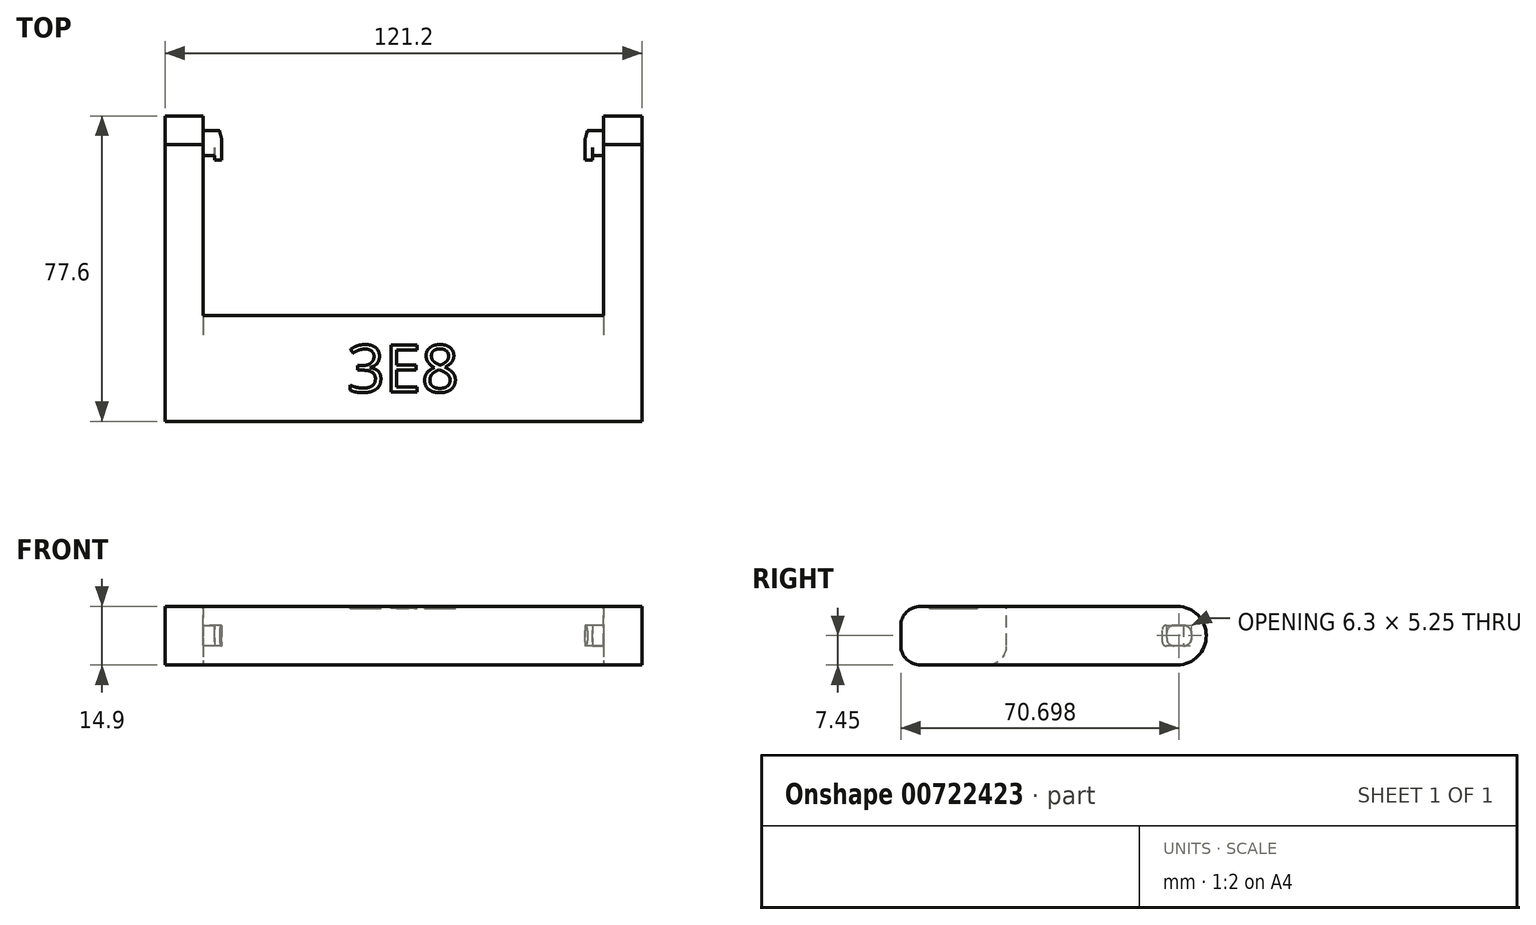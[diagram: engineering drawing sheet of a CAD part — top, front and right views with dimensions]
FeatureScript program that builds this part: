
annotation { "Feature Type Name" : "Feature", "Feature Type Description" : "" }
export const myFeature = defineFeature(function(context is Context, id is Id, definition is map)
    precondition{}
    {
        {
            var Q0;
            Q0=qCreatedBy(makeId("Top.planeOp"),FACE);
            var sketch = newSketch(context, id + "F0", { "sketchPlane" : qUnion([Q0])});
            skLineSegment(sketch, "E0.bottom", {"start": v(60.6, -38.8) * mm, "end": v(-60.6, -38.8) * mm});
            skLineSegment(sketch, "E0.top", {"start": v(60.6, 38.8) * mm, "end": v(-60.6, 38.8) * mm});
            skLineSegment(sketch, "E0.left", {"start": v(60.6, -38.8) * mm, "end": v(60.6, 38.8) * mm});
            skLineSegment(sketch, "E0.right", {"start": v(-60.6, -38.8) * mm, "end": v(-60.6, 38.8) * mm});
            skPoint(sketch, "E0.middle", {"position": v(0, 0) * mm});
            skSolve(sketch);
        }
        {
            var Q0;
            Q0 = qSketchRegion(id + "F0", true);
            extrude(context, id + "F1", {"entities" : qUnion([Q0]), "depth" : 14.9 * mm, "offsetDistance" : 25 * mm});
        }
        {
            var Q0;
            Q0=makeQuery(id+"F1.opExtrude","CAP_FACE",FACE,{"disambiguationData":[OSD([sQuery(id+"F0.wireOp",EDGE,"E0.bottom"),sQuery(id+"F0.wireOp",EDGE,"E0.top"),sQuery(id+"F0.wireOp",EDGE,"E0.left"),sQuery(id+"F0.wireOp",EDGE,"E0.right")])],"isStart":false});
            var sketch = newSketch(context, id + "F2", { "sketchPlane" : qUnion([Q0])});
            skLineSegment(sketch, "E1.bottom", {"start": v(-50.9, 38.8) * mm, "end": v(50.9, 38.8) * mm});
            skLineSegment(sketch, "E1.top", {"start": v(-50.9, -11.9) * mm, "end": v(50.9, -11.9) * mm});
            skLineSegment(sketch, "E1.left", {"start": v(-50.9, 38.8) * mm, "end": v(-50.9, -11.9) * mm});
            skLineSegment(sketch, "E1.right", {"start": v(50.9, 38.8) * mm, "end": v(50.9, -11.9) * mm});
            skPoint(sketch, "E1.middle", {"position": v(0, 13.45) * mm});
            skSolve(sketch);
        }
        {
            var Q0;
            Q0 = qSketchRegion(id + "F2", true);
            extrude(context, id + "F3", {"entities" : qUnion([Q0]), "operationType" : NewBodyOperationType.REMOVE, "endBound" : BoundingType.THROUGH_ALL, "oppositeDirection" : true, "depth" : 25 * mm, "offsetDistance" : 25 * mm});
        }
        {
            var Q0;
            Q0=makeQuery(id+"F3.boolean.opBoolean","COPY",FACE,{"derivedFrom":makeQuery(id+"F3.opExtrude","SWEPT_FACE",FACE,{"disambiguationData":[OSD([sQuery(id+"F2.wireOp",EDGE,"E1.left")])]})});
            var sketch = newSketch(context, id + "F4", { "sketchPlane" : qUnion([Q0])});
            skLineSegment(sketch, "E2.0", {"start": v(38.8, 0) * mm, "end": v(38.8, 14.9) * mm});
            skArc(sketch, "E3", {"start": v(31.18, 0) * mm, "mid": v(38.8, 7.29) * mm, "end": v(31.51, 14.9) * mm});
            skLineSegment(sketch, "E4", {"start": v(31.51, 14.9) * mm, "end": v(31.18, 0) * mm, "construction": true});
            skLineSegment(sketch, "E5", {"start": v(38.8, 14.9) * mm, "end": v(31.51, 14.9) * mm});
            skLineSegment(sketch, "E6", {"start": v(38.8, 0) * mm, "end": v(31.18, 0) * mm});
            skSolve(sketch);
        }
        {
            var Q0;
            Q0 = qSketchRegion(id + "F4", true);
            extrude(context, id + "F5", {"entities" : qUnion([Q0]), "operationType" : NewBodyOperationType.REMOVE, "endBound" : BoundingType.THROUGH_ALL, "oppositeDirection" : true, "depth" : 25 * mm, "offsetDistance" : 25 * mm, "hasSecondDirection" : true, "secondDirectionBound" : SecondDirectionBoundingType.THROUGH_ALL, "secondDirectionOppositeDirection" : false, "secondDirectionDepth" : 25 * mm});
        }
        {
            var Q0;
            Q0=makeQuery(id+"F3.boolean.opBoolean","COPY",EDGE,{"derivedFrom":makeQuery(id+"F3.opExtrude","CAP_EDGE",EDGE,{"disambiguationData":[OSD([sQuery(id+"F2.wireOp",EDGE,"E1.top")])],"isStart":true})});
            var Q1;
            Q1=makeQuery(id+"F3.boolean.opBoolean","INTERSECT",EDGE,{"derivedFrom":[makeQuery(id+"F1.opExtrude","CAP_FACE",FACE,{"disambiguationData":[OSD([sQuery(id+"F0.wireOp",EDGE,"E0.bottom"),sQuery(id+"F0.wireOp",EDGE,"E0.top"),sQuery(id+"F0.wireOp",EDGE,"E0.left"),sQuery(id+"F0.wireOp",EDGE,"E0.right")])],"isStart":true}),makeQuery(id+"F3.opExtrude","SWEPT_FACE",FACE,{"disambiguationData":[OSD([sQuery(id+"F2.wireOp",EDGE,"E1.top")])]})]});
            var Q2;
            Q2=makeQuery(id+"F1.opExtrude","CAP_EDGE",EDGE,{"disambiguationData":[OSD([sQuery(id+"F0.wireOp",EDGE,"E0.bottom")])],"isStart":false});
            var Q3;
            Q3=makeQuery(id+"F1.opExtrude","CAP_EDGE",EDGE,{"disambiguationData":[OSD([sQuery(id+"F0.wireOp",EDGE,"E0.bottom")])],"isStart":true});
            fillet(context, id + "F6", {"entities" : qUnion([Q0, Q1, Q2, Q3]), "radius" : 5 * mm, "tangentPropagation" : true, "allowEdgeOverflow" : false});
        }
        {
            var Q0;
            Q0=makeQuery(id+"F3.boolean.opBoolean","COPY",FACE,{"derivedFrom":makeQuery(id+"F3.opExtrude","SWEPT_FACE",FACE,{"disambiguationData":[OSD([sQuery(id+"F2.wireOp",EDGE,"E1.left")])]})});
            var sketch = newSketch(context, id + "F7", { "sketchPlane" : qUnion([Q0])});
            skLineSegment(sketch, "E7", {"start": v(31.51, 14.9) * mm, "end": v(31.51, 0) * mm, "construction": true});
            skLineSegment(sketch, "E8.bottom", {"start": v(35.05, 4.83) * mm, "end": v(27.65, 4.83) * mm});
            skLineSegment(sketch, "E8.top", {"start": v(35.05, 10.08) * mm, "end": v(27.65, 10.08) * mm});
            skLineSegment(sketch, "E8.left", {"start": v(35.05, 4.83) * mm, "end": v(35.05, 10.08) * mm});
            skLineSegment(sketch, "E8.right", {"start": v(27.65, 4.83) * mm, "end": v(27.65, 10.08) * mm});
            skPoint(sketch, "E8.middle", {"position": v(31.35, 7.45) * mm});
            skSolve(sketch);
        }
        {
            var Q0;
            Q0 = qSketchRegion(id + "F7", true);
            var Q1;
            Q1=makeQuery(id+"F3.boolean.opBoolean","COPY",FACE,{"derivedFrom":makeQuery(id+"F3.opExtrude","SWEPT_FACE",FACE,{"disambiguationData":[OSD([sQuery(id+"F2.wireOp",EDGE,"E1.right")])]})});
            extrude(context, id + "F8", {"entities" : qUnion([Q0]), "operationType" : NewBodyOperationType.ADD, "endBound" : BoundingType.UP_TO_SURFACE, "depth" : 25 * mm, "endBoundEntityFace" : qUnion([Q1]), "offsetDistance" : 25 * mm});
        }
        {
            var Q0;
            Q0=makeQuery(id+"F8.opExtrude","SWEPT_FACE",FACE,{"disambiguationData":[OSD([sQuery(id+"F7.wireOp",EDGE,"E8.top")])]});
            var sketch = newSketch(context, id + "F9", { "sketchPlane" : qUnion([Q0])});
            skLineSegment(sketch, "E9.bottom", {"start": v(46.2, 27.65) * mm, "end": v(-46.2, 27.65) * mm});
            skLineSegment(sketch, "E9.top", {"start": v(46.2, 35.05) * mm, "end": v(-46.2, 35.05) * mm});
            skLineSegment(sketch, "E9.left", {"start": v(46.2, 27.65) * mm, "end": v(46.2, 35.05) * mm});
            skLineSegment(sketch, "E9.right", {"start": v(-46.2, 27.65) * mm, "end": v(-46.2, 35.05) * mm});
            skPoint(sketch, "E9.middle", {"position": v(0, 31.35) * mm});
            skLineSegment(sketch, "E10", {"start": v(0, 35.05) * mm, "end": v(0, 27.65) * mm, "construction": true});
            skLineSegment(sketch, "E11.bottom", {"start": v(-50.9, 27.65) * mm, "end": v(-48, 27.65) * mm});
            skLineSegment(sketch, "E11.top", {"start": v(-50.9, 28.75) * mm, "end": v(-48, 28.75) * mm});
            skLineSegment(sketch, "E11.left", {"start": v(-50.9, 27.65) * mm, "end": v(-50.9, 28.75) * mm});
            skLineSegment(sketch, "E11.right", {"start": v(-48, 27.65) * mm, "end": v(-48, 28.75) * mm});
            skLineSegment(sketch, "E12.MirrorCS", {"start": v(50.9, 27.65) * mm, "end": v(50.9, 28.75) * mm});
            skLineSegment(sketch, "E13.MirrorCS", {"start": v(50.9, 28.75) * mm, "end": v(48, 28.75) * mm});
            skLineSegment(sketch, "E14.MirrorCS", {"start": v(48, 27.65) * mm, "end": v(48, 28.75) * mm});
            skLineSegment(sketch, "E15.MirrorCS", {"start": v(50.9, 27.65) * mm, "end": v(48, 27.65) * mm});
            skSolve(sketch);
        }
        {
            var Q0;
            Q0 = qSketchRegion(id + "F9", true);
            extrude(context, id + "F10", {"entities" : qUnion([Q0]), "operationType" : NewBodyOperationType.REMOVE, "endBound" : BoundingType.THROUGH_ALL, "oppositeDirection" : true, "depth" : 25 * mm, "offsetDistance" : 25 * mm});
        }
        {
            var Q0;
            {var subQ0=sQuery(id+"F7.wireOp",EDGE,"E8.left");var subQ1=sQuery(id+"F7.wireOp",EDGE,"E8.top");Q0=makeQuery(id+"F10.boolean.opBoolean","SPLIT",EDGE,{"disambiguationData":[TD([makeQuery(id+"F3.boolean.opBoolean","COPY",FACE,{"derivedFrom":makeQuery(id+"F3.opExtrude","SWEPT_FACE",FACE,{"disambiguationData":[OSD([sQuery(id+"F2.wireOp",EDGE,"E1.left")])]})})])],"derivedFrom":makeQuery(id+"F8.opExtrude","SWEPT_EDGE",EDGE,{"disambiguationData":[OSD([subQ1,subQ0])]})});}
            var Q1;
            {var subQ0=sQuery(id+"F7.wireOp",EDGE,"E8.left");var subQ1=sQuery(id+"F7.wireOp",EDGE,"E8.bottom");Q1=makeQuery(id+"F10.boolean.opBoolean","SPLIT",EDGE,{"disambiguationData":[TD([makeQuery(id+"F3.boolean.opBoolean","COPY",FACE,{"derivedFrom":makeQuery(id+"F3.opExtrude","SWEPT_FACE",FACE,{"disambiguationData":[OSD([sQuery(id+"F2.wireOp",EDGE,"E1.left")])]})})])],"derivedFrom":makeQuery(id+"F8.opExtrude","SWEPT_EDGE",EDGE,{"disambiguationData":[OSD([subQ1,subQ0])]})});}
            var Q2;
            Q2=makeQuery(id+"F10.boolean.opBoolean","COPY",EDGE,{"derivedFrom":makeQuery(id+"F10.opExtrude","CAP_EDGE",EDGE,{"disambiguationData":[OSD([sQuery(id+"F9.wireOp",EDGE,"E11.top")])],"isStart":true})});
            var Q3;
            Q3=makeQuery(id+"F10.boolean.opBoolean","INTERSECT",EDGE,{"derivedFrom":[makeQuery(id+"F8.opExtrude","SWEPT_FACE",FACE,{"disambiguationData":[OSD([sQuery(id+"F7.wireOp",EDGE,"E8.bottom")])]}),makeQuery(id+"F10.opExtrude","SWEPT_FACE",FACE,{"disambiguationData":[OSD([sQuery(id+"F9.wireOp",EDGE,"E11.top")])]})]});
            var Q4;
            Q4=makeQuery(id+"F10.boolean.opBoolean","COPY",EDGE,{"derivedFrom":makeQuery(id+"F10.opExtrude","CAP_EDGE",EDGE,{"disambiguationData":[OSD([sQuery(id+"F9.wireOp",EDGE,"E13.MirrorCS")])],"isStart":true})});
            var Q5;
            {var subQ0=sQuery(id+"F7.wireOp",EDGE,"E8.top");var subQ1=sQuery(id+"F7.wireOp",EDGE,"E8.left");Q5=makeQuery(id+"F10.boolean.opBoolean","SPLIT",EDGE,{"disambiguationData":[TD([makeQuery(id+"F3.boolean.opBoolean","COPY",FACE,{"derivedFrom":makeQuery(id+"F3.opExtrude","SWEPT_FACE",FACE,{"disambiguationData":[OSD([sQuery(id+"F2.wireOp",EDGE,"E1.right")])]})})])],"derivedFrom":makeQuery(id+"F8.opExtrude","SWEPT_EDGE",EDGE,{"disambiguationData":[OSD([subQ0,subQ1])]})});}
            var Q6;
            {var subQ0=sQuery(id+"F7.wireOp",EDGE,"E8.bottom");var subQ1=sQuery(id+"F7.wireOp",EDGE,"E8.left");Q6=makeQuery(id+"F10.boolean.opBoolean","SPLIT",EDGE,{"disambiguationData":[TD([makeQuery(id+"F3.boolean.opBoolean","COPY",FACE,{"derivedFrom":makeQuery(id+"F3.opExtrude","SWEPT_FACE",FACE,{"disambiguationData":[OSD([sQuery(id+"F2.wireOp",EDGE,"E1.right")])]})})])],"derivedFrom":makeQuery(id+"F8.opExtrude","SWEPT_EDGE",EDGE,{"disambiguationData":[OSD([subQ0,subQ1])]})});}
            var Q7;
            Q7=makeQuery(id+"F10.boolean.opBoolean","INTERSECT",EDGE,{"derivedFrom":[makeQuery(id+"F8.opExtrude","SWEPT_FACE",FACE,{"disambiguationData":[OSD([sQuery(id+"F7.wireOp",EDGE,"E8.bottom")])]}),makeQuery(id+"F10.opExtrude","SWEPT_FACE",FACE,{"disambiguationData":[OSD([sQuery(id+"F9.wireOp",EDGE,"E13.MirrorCS")])]})]});
            fillet(context, id + "F11", {"entities" : qUnion([Q0, Q1, Q2, Q3, Q4, Q5, Q6, Q7]), "radius" : 2 * mm, "tangentPropagation" : true, "allowEdgeOverflow" : false});
        }
        {
            var Q0;
            {var subQ0=sQuery(id+"F7.wireOp",EDGE,"E8.bottom");var subQ1=sQuery(id+"F7.wireOp",EDGE,"E8.right");Q0=makeQuery(id+"F10.boolean.opBoolean","SPLIT",EDGE,{"disambiguationData":[TD([makeQuery(id+"F10.opExtrude","SWEPT_FACE",FACE,{"disambiguationData":[OSD([sQuery(id+"F9.wireOp",EDGE,"E9.right")])]})])],"derivedFrom":makeQuery(id+"F8.opExtrude","SWEPT_EDGE",EDGE,{"disambiguationData":[OSD([subQ0,subQ1])]})});}
            var Q1;
            {var subQ0=sQuery(id+"F7.wireOp",EDGE,"E8.top");var subQ1=sQuery(id+"F7.wireOp",EDGE,"E8.right");Q1=makeQuery(id+"F10.boolean.opBoolean","SPLIT",EDGE,{"disambiguationData":[TD([makeQuery(id+"F10.opExtrude","SWEPT_FACE",FACE,{"disambiguationData":[OSD([sQuery(id+"F9.wireOp",EDGE,"E9.right")])]})])],"derivedFrom":makeQuery(id+"F8.opExtrude","SWEPT_EDGE",EDGE,{"disambiguationData":[OSD([subQ0,subQ1])]})});}
            var Q2;
            {var subQ0=sQuery(id+"F7.wireOp",EDGE,"E8.bottom");var subQ1=sQuery(id+"F7.wireOp",EDGE,"E8.right");Q2=makeQuery(id+"F10.boolean.opBoolean","SPLIT",EDGE,{"disambiguationData":[TD([makeQuery(id+"F10.opExtrude","SWEPT_FACE",FACE,{"disambiguationData":[OSD([sQuery(id+"F9.wireOp",EDGE,"E9.left")])]})])],"derivedFrom":makeQuery(id+"F8.opExtrude","SWEPT_EDGE",EDGE,{"disambiguationData":[OSD([subQ0,subQ1])]})});}
            var Q3;
            {var subQ0=sQuery(id+"F7.wireOp",EDGE,"E8.top");var subQ1=sQuery(id+"F7.wireOp",EDGE,"E8.right");Q3=makeQuery(id+"F10.boolean.opBoolean","SPLIT",EDGE,{"disambiguationData":[TD([makeQuery(id+"F10.opExtrude","SWEPT_FACE",FACE,{"disambiguationData":[OSD([sQuery(id+"F9.wireOp",EDGE,"E9.left")])]})])],"derivedFrom":makeQuery(id+"F8.opExtrude","SWEPT_EDGE",EDGE,{"disambiguationData":[OSD([subQ0,subQ1])]})});}
            fillet(context, id + "F12", {"entities" : qUnion([Q0, Q1, Q2, Q3]), "radius" : 1 * mm, "tangentPropagation" : true, "allowEdgeOverflow" : false});
        }
        {
            var Q0;
            Q0=makeQuery(id+"F10.boolean.opBoolean","SPLIT",FACE,{"disambiguationData":[TD([makeQuery(id+"F3.boolean.opBoolean","COPY",FACE,{"derivedFrom":makeQuery(id+"F3.opExtrude","SWEPT_FACE",FACE,{"disambiguationData":[OSD([sQuery(id+"F2.wireOp",EDGE,"E1.left")])]})})])],"derivedFrom":makeQuery(id+"F8.opExtrude","SWEPT_FACE",FACE,{"disambiguationData":[OSD([sQuery(id+"F7.wireOp",EDGE,"E8.bottom")])]})});
            var sketch = newSketch(context, id + "F13", { "sketchPlane" : qUnion([Q0])});
            skPoint(sketch, "E16.0", {"position": v(-46.2, -33.05) * mm});
            skLineSegment(sketch, "E17.0", {"start": v(-46.2, -35.05) * mm, "end": v(-50.9, -35.05) * mm});
            skLineSegment(sketch, "E18", {"start": v(-46.2, -33.05) * mm, "end": v(-46.2, -35.05) * mm});
            skLineSegment(sketch, "E19", {"start": v(-46.2, -33.05) * mm, "end": v(-46.74, -35.05) * mm});
            skLineSegment(sketch, "E20", {"start": v(0, 0) * mm, "end": v(0, -35.05) * mm, "construction": true});
            skLineSegment(sketch, "E21.MirrorCS", {"start": v(46.2, -35.05) * mm, "end": v(50.9, -35.05) * mm});
            skLineSegment(sketch, "E22.MirrorCS", {"start": v(46.2, -33.05) * mm, "end": v(46.74, -35.05) * mm});
            skLineSegment(sketch, "E23.MirrorCS", {"start": v(46.2, -33.05) * mm, "end": v(46.2, -35.05) * mm});
            skSolve(sketch);
        }
        {
            var Q0;
            Q0 = qSketchRegion(id + "F13", true);
            extrude(context, id + "F14", {"entities" : qUnion([Q0]), "operationType" : NewBodyOperationType.REMOVE, "endBound" : BoundingType.THROUGH_ALL, "oppositeDirection" : true, "depth" : 25 * mm, "offsetDistance" : 25 * mm});
        }
        {
            var Q0;
            Q0=makeQuery(id+"F1.opExtrude","CAP_FACE",FACE,{"disambiguationData":[OSD([sQuery(id+"F0.wireOp",EDGE,"E0.bottom"),sQuery(id+"F0.wireOp",EDGE,"E0.top"),sQuery(id+"F0.wireOp",EDGE,"E0.left"),sQuery(id+"F0.wireOp",EDGE,"E0.right")])],"isStart":false});
            var sketch = newSketch(context, id + "F15", { "sketchPlane" : qUnion([Q0])});
            skLineSegment(sketch, "E24", {"start": v(-50.9, -16.9) * mm, "end": v(50.9, -33.8) * mm, "construction": true});
            skText(sketch, "E25", { "text": "3E8", "fontName": "OpenSans-Regular.ttf"});
            skPoint(sketch, "E26", {"position": v(0, -25.35) * mm});
            const initialGuessF15  = {"E25": [-0.01427, -0.03135, 1, 0, 0.012]};
            skSetInitialGuess(sketch, initialGuessF15);
            skSolve(sketch);
        }
        {
            var Q0;
            Q0 = qSketchRegion(id + "F15", true);
            extrude(context, id + "F16", {"entities" : qUnion([Q0]), "operationType" : NewBodyOperationType.REMOVE, "oppositeDirection" : true, "depth" : .5 * mm, "offsetDistance" : 25 * mm});
        }
    });
